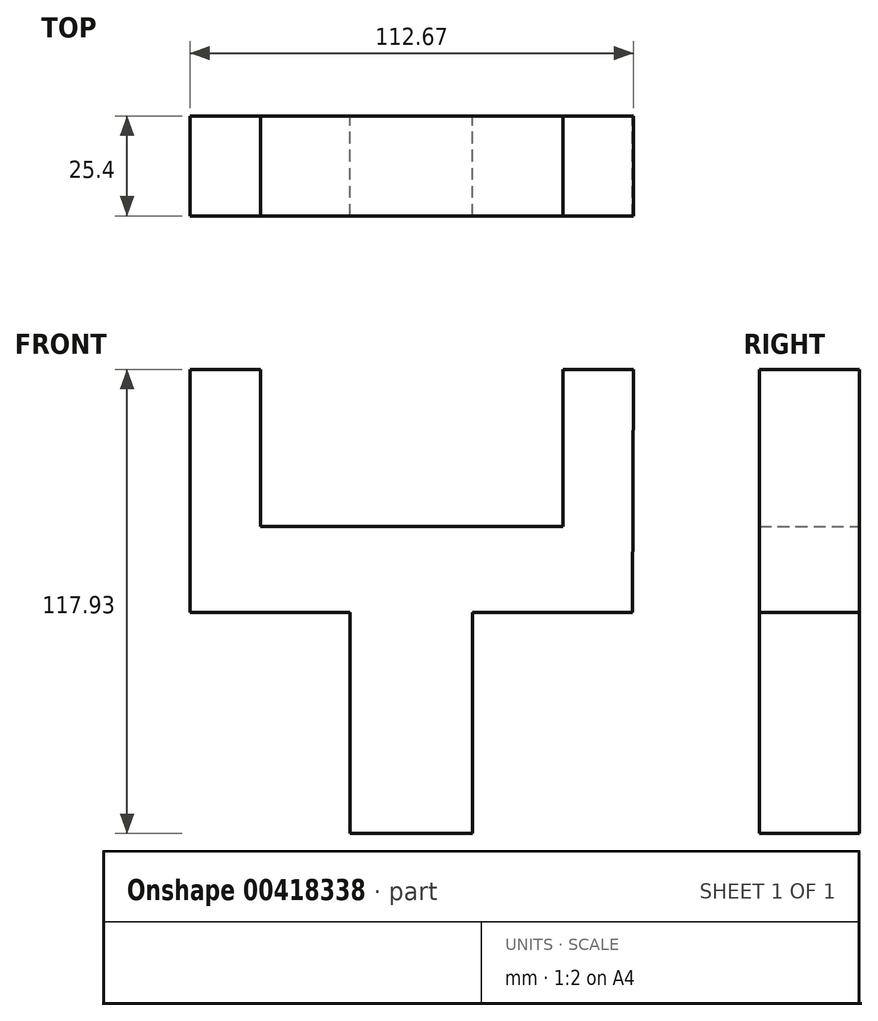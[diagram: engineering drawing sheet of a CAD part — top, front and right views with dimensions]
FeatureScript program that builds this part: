
annotation { "Feature Type Name" : "Feature", "Feature Type Description" : "" }
export const myFeature = defineFeature(function(context is Context, id is Id, definition is map)
    precondition{}
    {
        {
            var Q0;
            Q0=qCreatedBy(makeId("Front.planeOp"),FACE);
            var sketch = newSketch(context, id + "F0", { "sketchPlane" : qUnion([Q0])});
            skLineSegment(sketch, "E0.left", {"start": v(-58.8, 21.82) * mm, "end": v(-58.8, 0) * mm});
            skLineSegment(sketch, "E0.right", {"start": v(53.64, 21.82) * mm, "end": v(53.64, 0) * mm});
            skLineSegment(sketch, "E1.top", {"start": v(35.9, 61.75) * mm, "end": v(53.86, 61.75) * mm});
            skLineSegment(sketch, "E1.left", {"start": v(35.9, 21.82) * mm, "end": v(35.9, 61.75) * mm});
            skLineSegment(sketch, "E1.right", {"start": v(53.86, 21.82) * mm, "end": v(53.86, 61.75) * mm});
            skLineSegment(sketch, "E2.bottom", {"start": v(-157.23, 67.01) * mm, "end": v(-151.97, 67.01) * mm});
            skLineSegment(sketch, "E2.top", {"start": v(-157.23, 71.96) * mm, "end": v(-151.97, 71.96) * mm});
            skLineSegment(sketch, "E2.left", {"start": v(-157.23, 67.01) * mm, "end": v(-157.23, 71.96) * mm});
            skLineSegment(sketch, "E2.right", {"start": v(-151.97, 67.01) * mm, "end": v(-151.97, 71.96) * mm});
            skLineSegment(sketch, "E3", {"start": v(-58.8, 21.82) * mm, "end": v(-58.8, 61.75) * mm});
            skLineSegment(sketch, "E4", {"start": v(-58.8, 61.75) * mm, "end": v(-40.86, 61.75) * mm});
            skLineSegment(sketch, "E5", {"start": v(-40.86, 61.75) * mm, "end": v(-40.86, 21.82) * mm});
            skLineSegment(sketch, "E6", {"start": v(-40.86, 21.82) * mm, "end": v(35.9, 21.82) * mm});
            skLineSegment(sketch, "E7", {"start": v(-58.8, 0) * mm, "end": v(-18.17, 0) * mm});
            skLineSegment(sketch, "E8", {"start": v(53.64, 0) * mm, "end": v(13, 0) * mm});
            skLineSegment(sketch, "E9.top", {"start": v(-18.17, -56.18) * mm, "end": v(13, -56.18) * mm});
            skLineSegment(sketch, "E9.left", {"start": v(-18.17, 0) * mm, "end": v(-18.17, -56.18) * mm});
            skLineSegment(sketch, "E9.right", {"start": v(13, 0) * mm, "end": v(13, -56.18) * mm});
            skLineSegment(sketch, "E10", {"start": v(-58.8, 61.75) * mm, "end": v(-58.8, 0) * mm});
            skLineSegment(sketch, "E11", {"start": v(13, -56.18) * mm, "end": v(13, 0) * mm});
            skLineSegment(sketch, "E12", {"start": v(53.64, 0) * mm, "end": v(53.86, 61.75) * mm});
            skLineSegment(sketch, "E13", {"start": v(35.9, 21.82) * mm, "end": v(-40.86, 21.82) * mm});
            skSolve(sketch);
        }
        {
            var Q0;
            Q0=makeQuery(id+"F0.imprint","IMPRINT",FACE,{"disambiguationData":[TD([[makeQuery(id+"F0.imprint","IMPRINT",EDGE,{"derivedFrom":sQuery(id+"F0.wireOp",EDGE,"E1.left")}),-1.0]])]});
            extrude(context, id + "F1", {"entities" : qUnion([Q0]), "depth" : 25.4 * mm});
        }
    });
